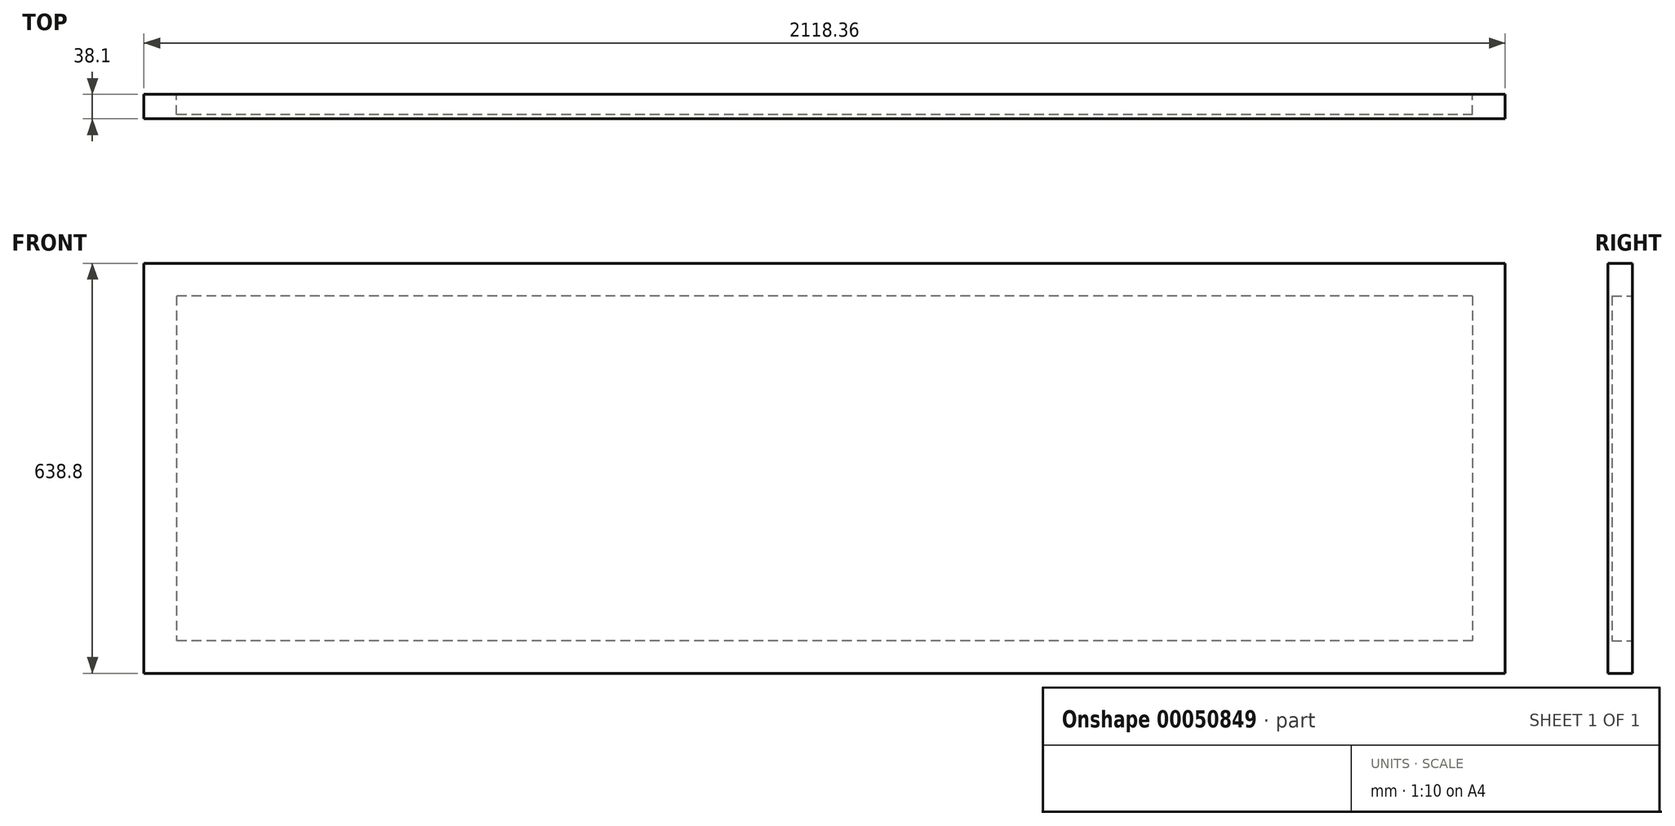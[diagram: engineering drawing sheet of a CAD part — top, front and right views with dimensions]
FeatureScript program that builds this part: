
annotation { "Feature Type Name" : "Feature", "Feature Type Description" : "" }
export const myFeature = defineFeature(function(context is Context, id is Id, definition is map)
    precondition{}
    {
        {
            var Q0;
            Q0=qCreatedBy(makeId("Front.planeOp"),FACE);
            var sketch = newSketch(context, id + "F0", { "sketchPlane" : qUnion([Q0])});
            skLineSegment(sketch, "E0.rect.bottom", {"start": v(-1059.18, 319.4) * mm, "end": v(1059.18, 319.4) * mm});
            skLineSegment(sketch, "E0.rect.top", {"start": v(-1059.18, -319.4) * mm, "end": v(1059.18, -319.4) * mm});
            skLineSegment(sketch, "E0.rect.left", {"start": v(-1059.18, 319.4) * mm, "end": v(-1059.18, -319.4) * mm});
            skLineSegment(sketch, "E0.rect.right", {"start": v(1059.18, 319.4) * mm, "end": v(1059.18, -319.4) * mm});
            skPoint(sketch, "E0.rect.middle", {"position": v(0, 0) * mm});
            skSolve(sketch);
        }
        {
            var Q0;
            Q0 = qSketchRegion(id + "F0", true);
            extrude(context, id + "F1", {"entities" : qUnion([Q0]), "depth" : 38.1 * mm});
        }
        {
            var Q0;
            Q0=makeQuery(id+"F1.opExtrude","CAP_FACE",FACE,{"disambiguationData":[OSD([sQuery(id+"F0.wireOp",EDGE,"E0.rect.bottom"),sQuery(id+"F0.wireOp",EDGE,"E0.rect.top"),sQuery(id+"F0.wireOp",EDGE,"E0.rect.left"),sQuery(id+"F0.wireOp",EDGE,"E0.rect.right")])],"isStart":true});
            var sketch = newSketch(context, id + "F2", { "sketchPlane" : qUnion([Q0])});
            skLineSegment(sketch, "E1.rect.bottom", {"start": v(-1008.38, 268.6) * mm, "end": v(1008.38, 268.6) * mm});
            skLineSegment(sketch, "E1.rect.top", {"start": v(-1008.38, -268.6) * mm, "end": v(1008.38, -268.6) * mm});
            skLineSegment(sketch, "E1.rect.left", {"start": v(-1008.38, 268.6) * mm, "end": v(-1008.38, -268.6) * mm});
            skLineSegment(sketch, "E1.rect.right", {"start": v(1008.38, 268.6) * mm, "end": v(1008.38, -268.6) * mm});
            skPoint(sketch, "E1.rect.middle", {"position": v(0, 0) * mm});
            skSolve(sketch);
        }
        {
            var Q0;
            Q0=makeQuery(id+"F2.imprint","IMPRINT",FACE,{"disambiguationData":[TD([[makeQuery(id+"F2.imprint","IMPRINT",EDGE,{"derivedFrom":sQuery(id+"F2.wireOp",EDGE,"E1.rect.bottom")}),-1.0]])]});
            extrude(context, id + "F3", {"entities" : qUnion([Q0]), "operationType" : NewBodyOperationType.REMOVE, "oppositeDirection" : true, "depth" : 31.75 * mm});
        }
    });
